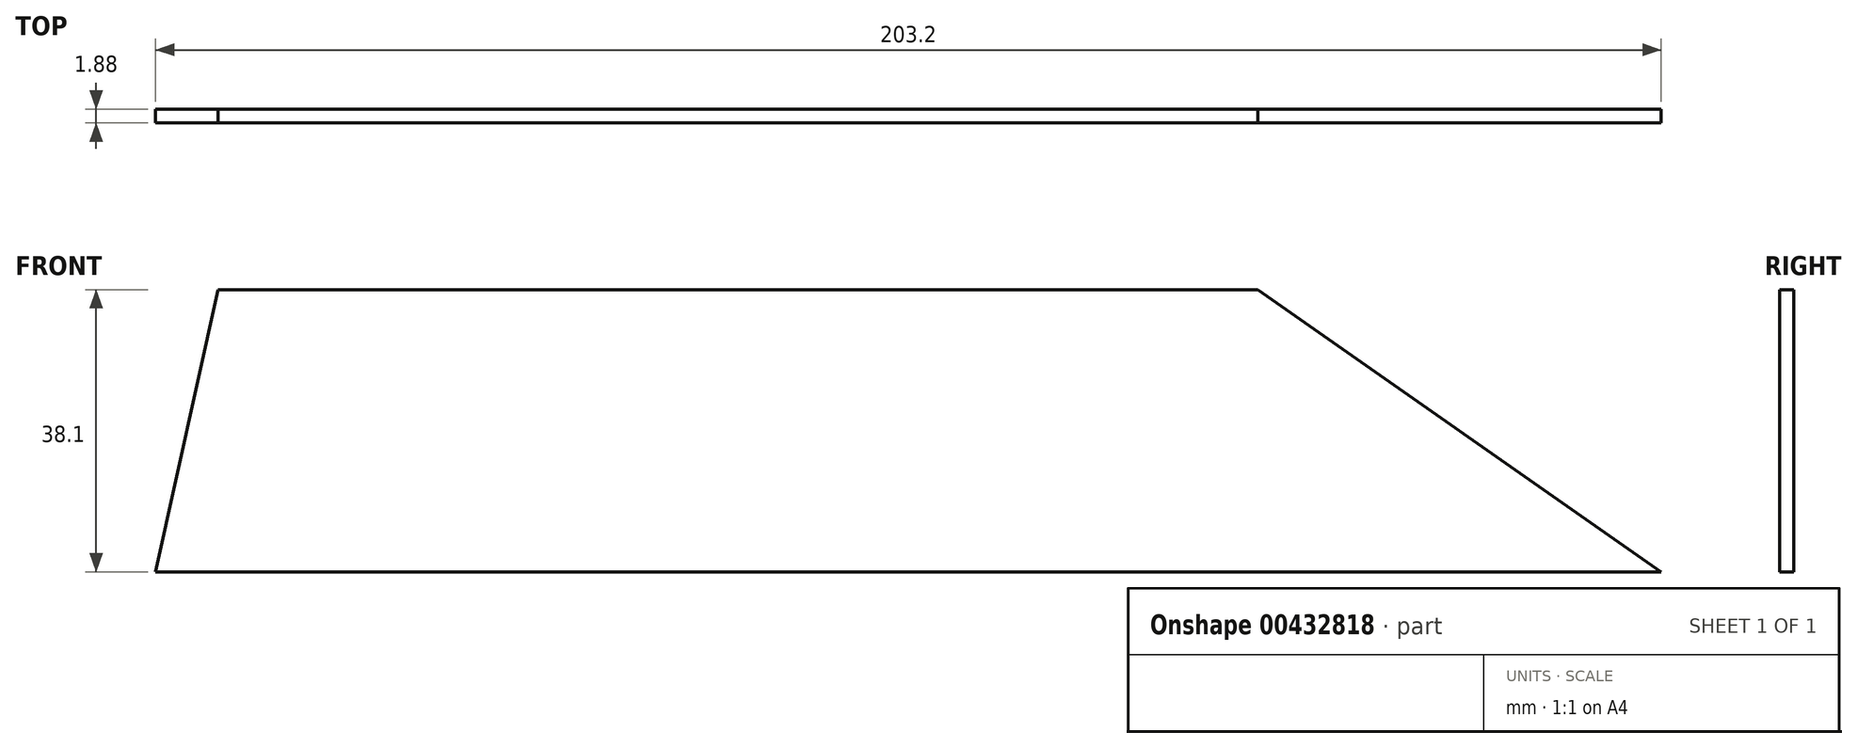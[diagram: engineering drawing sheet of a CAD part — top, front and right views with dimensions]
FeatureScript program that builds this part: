
annotation { "Feature Type Name" : "Feature", "Feature Type Description" : "" }
export const myFeature = defineFeature(function(context is Context, id is Id, definition is map)
    precondition{}
    {
        {
            var Q0;
            Q0=qCreatedBy(makeId("Front.planeOp"),FACE);
            var sketch = newSketch(context, id + "F0", { "sketchPlane" : qUnion([Q0])});
            skLineSegment(sketch, "E0.bottom", {"start": v(-93.15, 19.05) * mm, "end": v(47.19, 19.05) * mm});
            skLineSegment(sketch, "E0.top", {"start": v(-101.6, -19.05) * mm, "end": v(101.6, -19.05) * mm});
            skLineSegment(sketch, "E0.left", {"start": v(-101.6, 19.05) * mm, "end": v(-101.6, -19.05) * mm});
            skLineSegment(sketch, "E0.right", {"start": v(101.6, 19.05) * mm, "end": v(101.6, -19.05) * mm});
            skPoint(sketch, "E0.middle", {"position": v(0, 0) * mm});
            skLineSegment(sketch, "E1", {"start": v(-101.6, -19.05) * mm, "end": v(-93.15, 19.05) * mm});
            skLineSegment(sketch, "E2", {"start": v(101.6, -19.05) * mm, "end": v(47.19, 19.05) * mm});
            skSolve(sketch);
        }
        {
            var Q0;
            Q0 = qSketchRegion(id + "F0", true);
            extrude(context, id + "F1", {"entities" : qUnion([Q0]), "depth" : 1.88 * mm});
        }
    });
